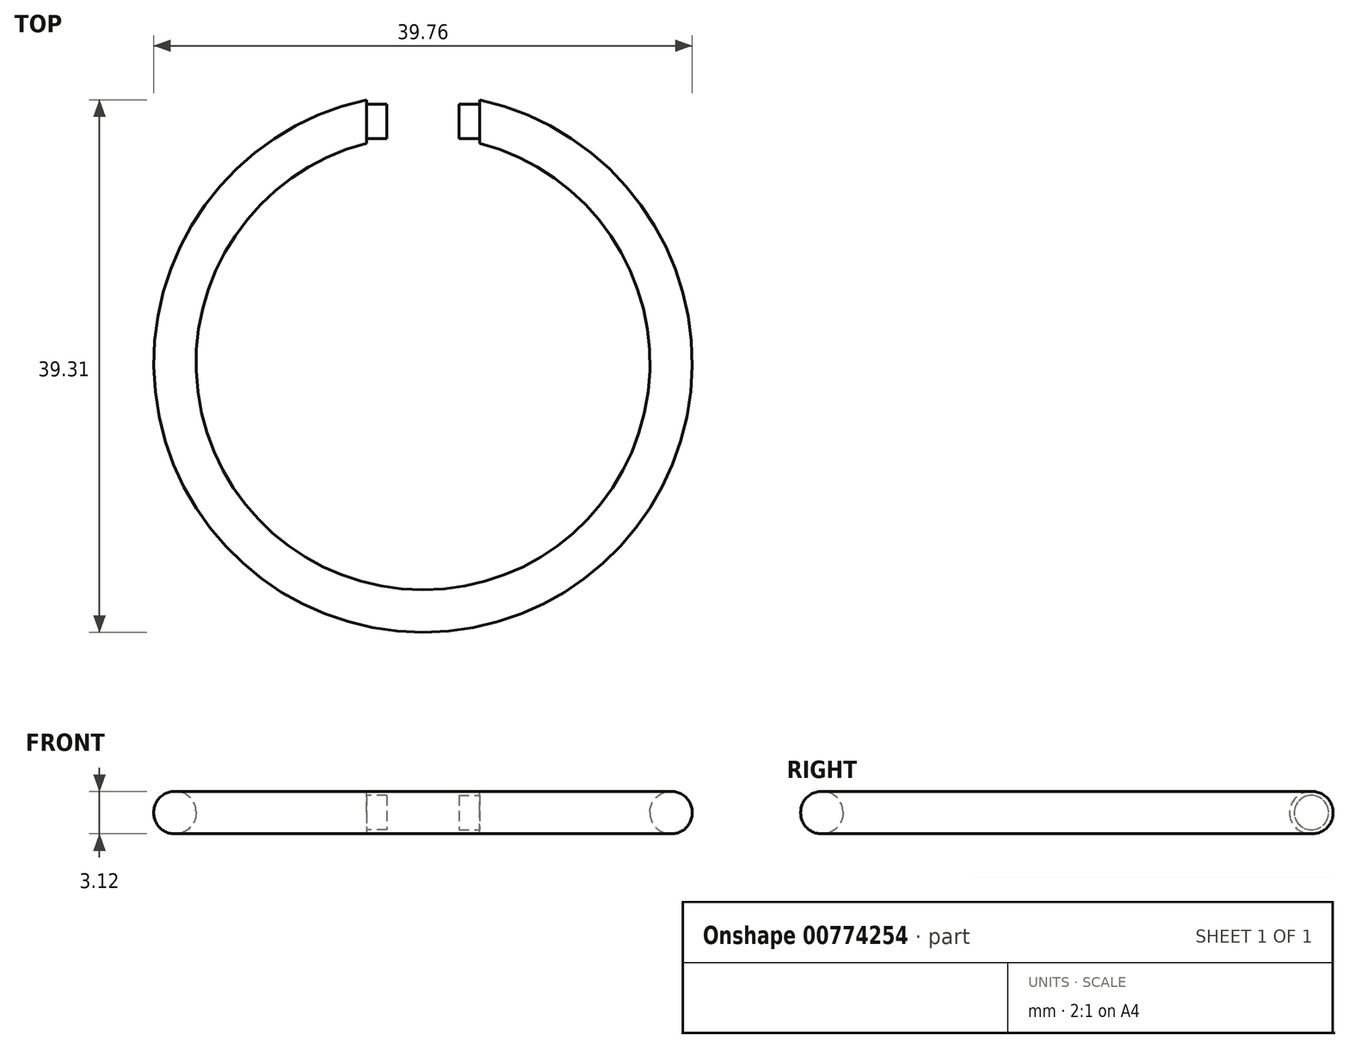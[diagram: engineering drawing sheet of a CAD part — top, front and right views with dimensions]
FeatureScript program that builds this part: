
annotation { "Feature Type Name" : "Feature", "Feature Type Description" : "" }
export const myFeature = defineFeature(function(context is Context, id is Id, definition is map)
    precondition{}
    {
        {
            var Q0;
            Q0=qCreatedBy(makeId("Top.planeOp"),FACE);
            var sketch = newSketch(context, id + "F0", { "sketchPlane" : qUnion([Q0])});
            skCircle(sketch, "E0", {"center": v(0, 0) * mm, "radius": 19.88 * mm});
            skCircle(sketch, "E1", {"center": v(0, 0) * mm, "radius": 16.75 * mm});
            skLineSegment(sketch, "E2", {"start": v(-4.18, 16.22) * mm, "end": v(-4.18, 19.43) * mm});
            skLineSegment(sketch, "E3", {"start": v(0, 21.7) * mm, "end": v(0, 12.81) * mm, "construction": true});
            skLineSegment(sketch, "E4.MirrorCS", {"start": v(4.18, 16.22) * mm, "end": v(4.18, 19.43) * mm});
            skSolve(sketch);
        }
        {
            var Q0;
            {var subQ0=sQuery(id+"F0.wireOp",EDGE,"E2");Q0=makeQuery(id+"F0.imprint","IMPRINT",FACE,{"disambiguationData":[TD([[makeQuery(id+"F0.imprint","IMPRINT",EDGE,{"derivedFrom":subQ0}),1.0]])]});}
            extrude(context, id + "F1", {"entities" : qUnion([Q0]), "depth" : 3.12 * mm, "offsetDistance" : 25.4 * mm});
        }
        {
            var Q0;
            Q0=makeQuery(id+"F1.opExtrude","SWEPT_FACE",FACE,{"disambiguationData":[OSD([sQuery(id+"F0.wireOp",EDGE,"E4.MirrorCS")])]});
            var sketch = newSketch(context, id + "F2", { "sketchPlane" : qUnion([Q0])});
            skLineSegment(sketch, "E5", {"start": v(-16.22, 1.56) * mm, "end": v(-19.43, 1.56) * mm});
            skCircle(sketch, "E6", {"center": v(-17.83, 1.56) * mm, "radius": 1.27 * mm});
            skSolve(sketch);
        }
        {
            var Q0;
            {var subQ0=sQuery(id+"F2.wireOp",EDGE,"E6");var subQ1=sQuery(id+"F2.wireOp",EDGE,"E5");var subQ2=makeQuery(id+"F2.imprint","INTERSECT",VERTEX,{"disambiguationData":[OD(0.0)],"derivedFrom":[subQ1,subQ0]});Q0=makeQuery(id+"F2.imprint","IMPRINT",FACE,{"disambiguationData":[TD([[makeQuery(id+"F2.imprint","IMPRINT",EDGE,{"disambiguationData":[TD([[subQ2,-1.0]])],"derivedFrom":subQ1}),-1.0]])]});}
            var Q1;
            {var subQ0=sQuery(id+"F2.wireOp",EDGE,"E6");var subQ1=sQuery(id+"F2.wireOp",EDGE,"E5");var subQ2=makeQuery(id+"F2.imprint","INTERSECT",VERTEX,{"disambiguationData":[OD(0.0)],"derivedFrom":[subQ1,subQ0]});Q1=makeQuery(id+"F2.imprint","IMPRINT",FACE,{"disambiguationData":[TD([[makeQuery(id+"F2.imprint","IMPRINT",EDGE,{"disambiguationData":[TD([[subQ2,-1.0]])],"derivedFrom":subQ1}),1.0]])]});}
            var Q2;
            Q2=sQuery(id+"F2.wireOp",EDGE,"E6");
            extrude(context, id + "F3", {"entities" : qUnion([Q0, Q1]), "operationType" : NewBodyOperationType.ADD, "surfaceEntities" : qUnion([Q2]), "depth" : 1.52 * mm, "offsetDistance" : 25.4 * mm});
        }
        {
            var Q0;
            Q0=makeQuery(id+"F1.opExtrude","SWEPT_FACE",FACE,{"disambiguationData":[OSD([sQuery(id+"F0.wireOp",EDGE,"E2")])]});
            var sketch = newSketch(context, id + "F4", { "sketchPlane" : qUnion([Q0])});
            skLineSegment(sketch, "E7", {"start": v(19.43, 1.56) * mm, "end": v(16.22, 1.56) * mm});
            skCircle(sketch, "E8", {"center": v(17.83, 1.56) * mm, "radius": 1.27 * mm});
            skSolve(sketch);
        }
        {
            var Q0;
            {var subQ0=sQuery(id+"F4.wireOp",EDGE,"E8");var subQ1=sQuery(id+"F4.wireOp",EDGE,"E7");var subQ2=makeQuery(id+"F4.imprint","INTERSECT",VERTEX,{"disambiguationData":[OD(0.0)],"derivedFrom":[subQ1,subQ0]});Q0=makeQuery(id+"F4.imprint","IMPRINT",FACE,{"disambiguationData":[TD([[makeQuery(id+"F4.imprint","IMPRINT",EDGE,{"disambiguationData":[TD([[subQ2,-1.0]])],"derivedFrom":subQ1}),1.0]])]});}
            var Q1;
            {var subQ0=sQuery(id+"F4.wireOp",EDGE,"E8");var subQ1=sQuery(id+"F4.wireOp",EDGE,"E7");var subQ2=makeQuery(id+"F4.imprint","INTERSECT",VERTEX,{"disambiguationData":[OD(0.0)],"derivedFrom":[subQ1,subQ0]});Q1=makeQuery(id+"F4.imprint","IMPRINT",FACE,{"disambiguationData":[TD([[makeQuery(id+"F4.imprint","IMPRINT",EDGE,{"disambiguationData":[TD([[subQ2,-1.0]])],"derivedFrom":subQ1}),-1.0]])]});}
            var Q2;
            Q2=sQuery(id+"F4.wireOp",EDGE,"E8");
            extrude(context, id + "F5", {"entities" : qUnion([Q0, Q1]), "operationType" : NewBodyOperationType.ADD, "surfaceEntities" : qUnion([Q2]), "depth" : 1.52 * mm, "offsetDistance" : 25.4 * mm});
        }
        {
            var Q0;
            Q0=makeQuery(id+"F1.opExtrude","CAP_EDGE",EDGE,{"disambiguationData":[OSD([sQuery(id+"F0.wireOp",EDGE,"E1")])],"isStart":false});
            var Q1;
            Q1=makeQuery(id+"F1.opExtrude","CAP_EDGE",EDGE,{"disambiguationData":[OSD([sQuery(id+"F0.wireOp",EDGE,"E0")])],"isStart":false});
            var Q2;
            Q2=makeQuery(id+"F1.opExtrude","CAP_EDGE",EDGE,{"disambiguationData":[OSD([sQuery(id+"F0.wireOp",EDGE,"E0")])],"isStart":true});
            var Q3;
            Q3=makeQuery(id+"F1.opExtrude","CAP_EDGE",EDGE,{"disambiguationData":[OSD([sQuery(id+"F0.wireOp",EDGE,"E1")])],"isStart":true});
            fillet(context, id + "F6", {"entities" : qUnion([Q0, Q1, Q2, Q3]), "radius" : 1.52 * mm, "tangentPropagation" : true, "allowEdgeOverflow" : false});
        }
    });
